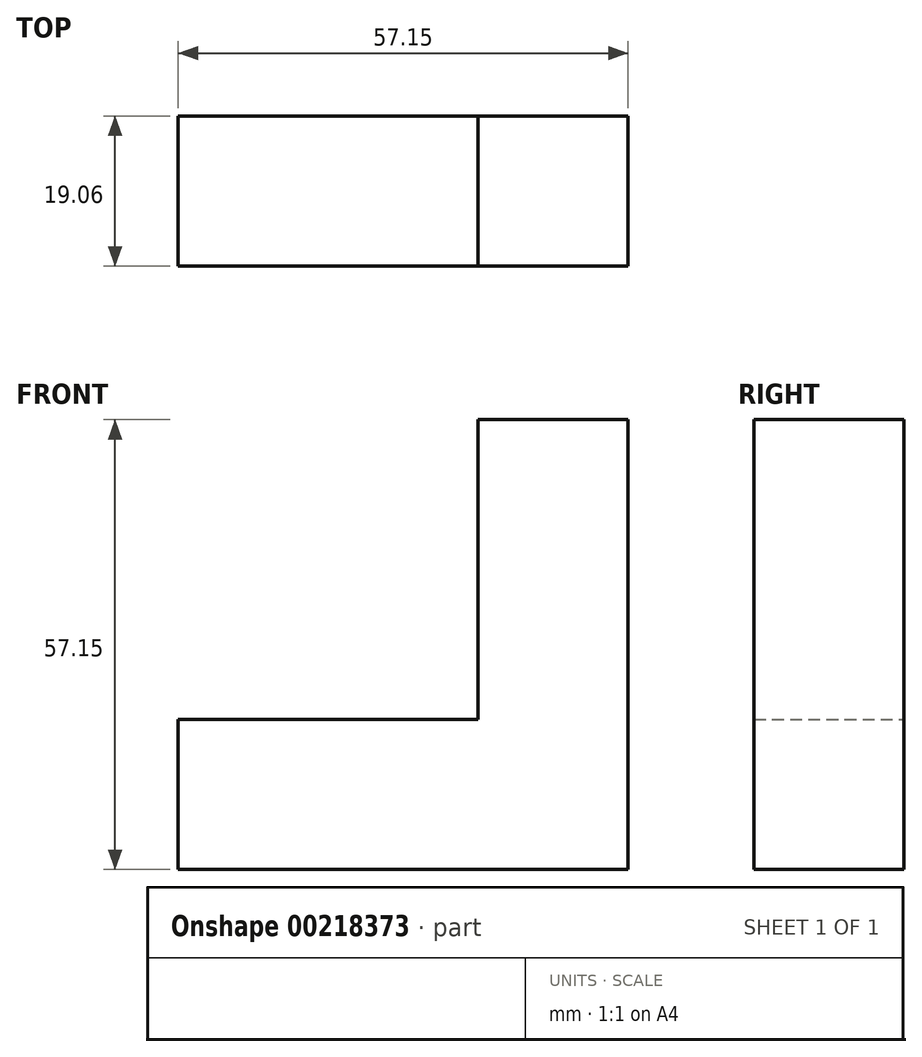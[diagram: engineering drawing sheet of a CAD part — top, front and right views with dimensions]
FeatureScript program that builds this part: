
annotation { "Feature Type Name" : "Feature", "Feature Type Description" : "" }
export const myFeature = defineFeature(function(context is Context, id is Id, definition is map)
    precondition{}
    {
        {
            var Q0;
            Q0=qCreatedBy(makeId("Front.planeOp"),FACE);
            var sketch = newSketch(context, id + "F0", { "sketchPlane" : qUnion([Q0])});
            skLineSegment(sketch, "E0.bottom", {"start": v(-56.9, -48.4) * mm, "end": v(0.25, -48.4) * mm});
            skLineSegment(sketch, "E0.top", {"start": v(-56.9, -29.36) * mm, "end": v(0.25, -29.36) * mm});
            skLineSegment(sketch, "E0.left", {"start": v(-56.9, -48.4) * mm, "end": v(-56.9, -29.36) * mm});
            skLineSegment(sketch, "E0.right", {"start": v(0.25, -48.4) * mm, "end": v(0.25, -29.36) * mm});
            skPoint(sketch, "E0.middle", {"position": v(-28.32, -38.88) * mm});
            skLineSegment(sketch, "E1", {"start": v(0.25, -29.36) * mm, "end": v(0.25, 8.74) * mm});
            skLineSegment(sketch, "E2", {"start": v(0.25, 8.74) * mm, "end": v(-18.8, 8.74) * mm});
            skLineSegment(sketch, "E3", {"start": v(-18.8, 8.74) * mm, "end": v(-18.8, -29.36) * mm});
            skSolve(sketch);
        }
        {
            var Q0;
            Q0 = qSketchRegion(id + "F0", true);
            extrude(context, id + "F1", {"entities" : qUnion([Q0]), "endBound" : BoundingType.SYMMETRIC, "depth" : 19.05 * mm});
        }
        {
            var Q0;
            Q0 = qSketchRegion(id + "F0", true);
            extrude(context, id + "F2", {"entities" : qUnion([Q0]), "operationType" : NewBodyOperationType.ADD, "endBound" : BoundingType.SYMMETRIC, "depth" : 19.05 * mm});
        }
    });
